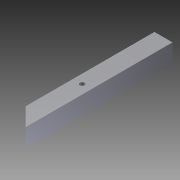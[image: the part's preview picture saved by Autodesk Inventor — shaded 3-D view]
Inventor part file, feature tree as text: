
AUTODESK INVENTOR PART (.ipt)
format: ipt  version: 2012 (Build 160160000, 160)  size: 97,280 bytes
history: native  units: in
note: dims shown in document units (in); Inventor stores cm internally (conversion verified against a paired STEP export)
features: extrude x3, sketch x3
ambient origin geometry x8: Origin, YZ Plane, XZ Plane, XY Plane, X Axis, Y Axis, Z Axis, Center Point
bodies: Solid1 (feature_tree)
feature tree (6):
  extrude  "Extrusion1"  Depth=1.0in
  extrude  "Extrusion4"  Depth=0.5in
  extrude  "Extrusion5"  Depth=0.125in
  sketch  "Sketch1"  dims[d0=1.0in d1=1.0in]
  sketch  "Sketch4"  dims[d2=0.5in d3=0.5in]
  sketch  "Sketch5"  dims[d4=0.125in d5=0.125in d6=0.125in d7=0.125in d8=8.125in d9=0.0in d16=45.0deg d17=1.0in d18=0.0in d19=4.5in d20=0.5in d21=0.25in d22=1.0in d23=0.0in]
